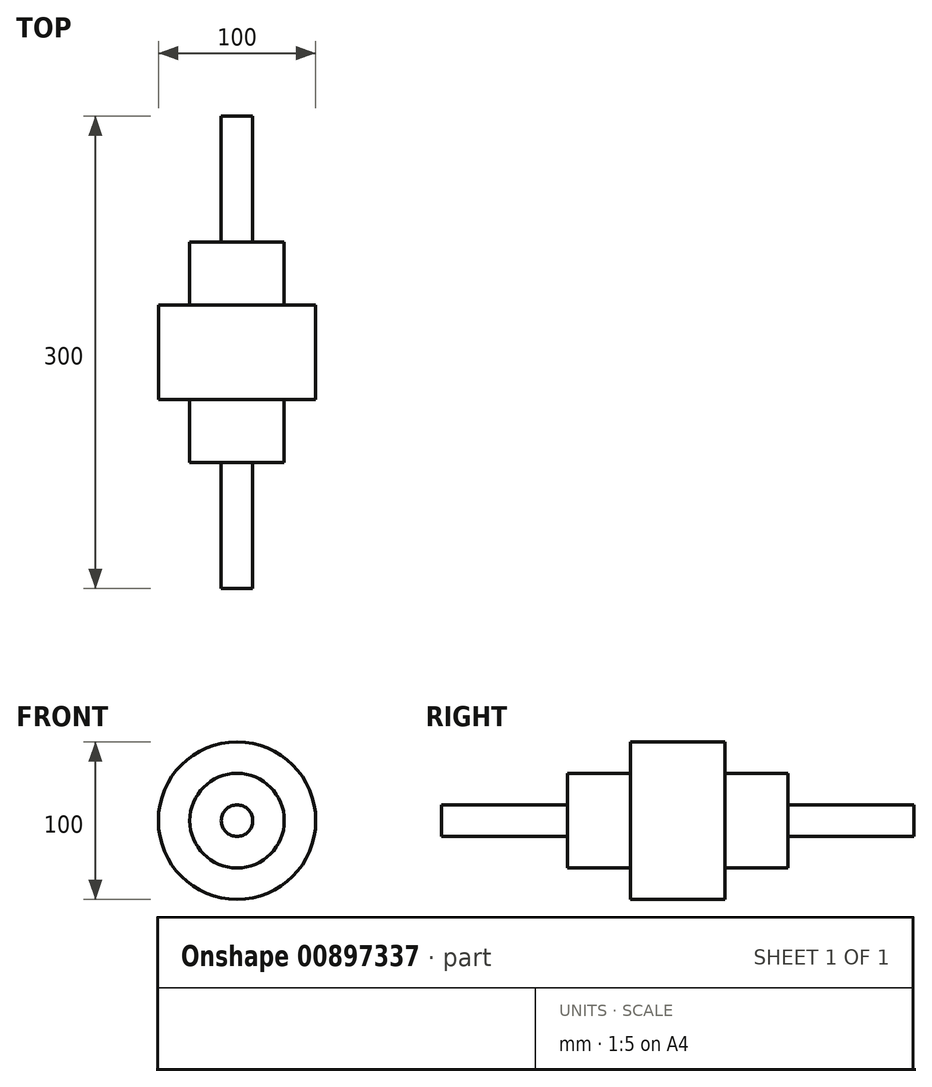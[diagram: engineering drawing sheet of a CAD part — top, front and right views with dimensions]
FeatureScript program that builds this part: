
annotation { "Feature Type Name" : "Feature", "Feature Type Description" : "" }
export const myFeature = defineFeature(function(context is Context, id is Id, definition is map)
    precondition{}
    {
        {
            var Q0;
            Q0=qCreatedBy(makeId("Front.planeOp"),FACE);
            var sketch = newSketch(context, id + "F0", { "sketchPlane" : qUnion([Q0])});
            skCircle(sketch, "E0", {"center": v(0, 0) * mm, "radius": 50 * mm});
            skSolve(sketch);
        }
        {
            var Q0;
            Q0 = qSketchRegion(id + "F0", true);
            extrude(context, id + "F1", {"entities" : qUnion([Q0]), "depth" : 30 * mm, "offsetDistance" : 25.4 * mm, "hasSecondDirection" : true, "secondDirectionOppositeDirection" : true, "secondDirectionDepth" : 30 * mm});
        }
        {
            var Q0;
            Q0=makeQuery(id+"F1.opExtrude","CAP_FACE",FACE,{"disambiguationData":[OSD([sQuery(id+"F0.wireOp",EDGE,"E0")])],"isStart":true});
            var sketch = newSketch(context, id + "F2", { "sketchPlane" : qUnion([Q0])});
            skCircle(sketch, "E1", {"center": v(0, 0) * mm, "radius": 30 * mm});
            skSolve(sketch);
        }
        {
            var Q0;
            Q0 = qSketchRegion(id + "F2", true);
            extrude(context, id + "F3", {"entities" : qUnion([Q0]), "operationType" : NewBodyOperationType.ADD, "depth" : 40 * mm, "offsetDistance" : 25.4 * mm});
        }
        {
            var Q0;
            Q0=makeQuery(id+"F1.opExtrude","CAP_FACE",FACE,{"disambiguationData":[OSD([sQuery(id+"F0.wireOp",EDGE,"E0")])],"isStart":false});
            var sketch = newSketch(context, id + "F4", { "sketchPlane" : qUnion([Q0])});
            skCircle(sketch, "E2", {"center": v(0, 0) * mm, "radius": 30 * mm});
            skSolve(sketch);
        }
        {
            var Q0;
            Q0 = qSketchRegion(id + "F4", true);
            extrude(context, id + "F5", {"entities" : qUnion([Q0]), "operationType" : NewBodyOperationType.ADD, "depth" : 40 * mm, "offsetDistance" : 25.4 * mm});
        }
        {
            var Q0;
            Q0=makeQuery(id+"F5.opExtrude","CAP_FACE",FACE,{"disambiguationData":[OSD([sQuery(id+"F4.wireOp",EDGE,"E2")])],"isStart":false});
            var sketch = newSketch(context, id + "F6", { "sketchPlane" : qUnion([Q0])});
            skCircle(sketch, "E3", {"center": v(0, 0) * mm, "radius": 10 * mm});
            skSolve(sketch);
        }
        {
            var Q0;
            Q0 = qSketchRegion(id + "F6", true);
            extrude(context, id + "F7", {"entities" : qUnion([Q0]), "operationType" : NewBodyOperationType.ADD, "depth" : 80 * mm, "offsetDistance" : 25.4 * mm});
        }
        {
            var Q0;
            Q0=makeQuery(id+"F3.opExtrude","CAP_FACE",FACE,{"disambiguationData":[OSD([sQuery(id+"F2.wireOp",EDGE,"E1")])],"isStart":false});
            var sketch = newSketch(context, id + "F8", { "sketchPlane" : qUnion([Q0])});
            skCircle(sketch, "E4", {"center": v(0, 0) * mm, "radius": 10 * mm});
            skSolve(sketch);
        }
        {
            var Q0;
            Q0 = qSketchRegion(id + "F8", true);
            extrude(context, id + "F9", {"entities" : qUnion([Q0]), "operationType" : NewBodyOperationType.ADD, "depth" : 80 * mm, "offsetDistance" : 25.4 * mm});
        }
    });
